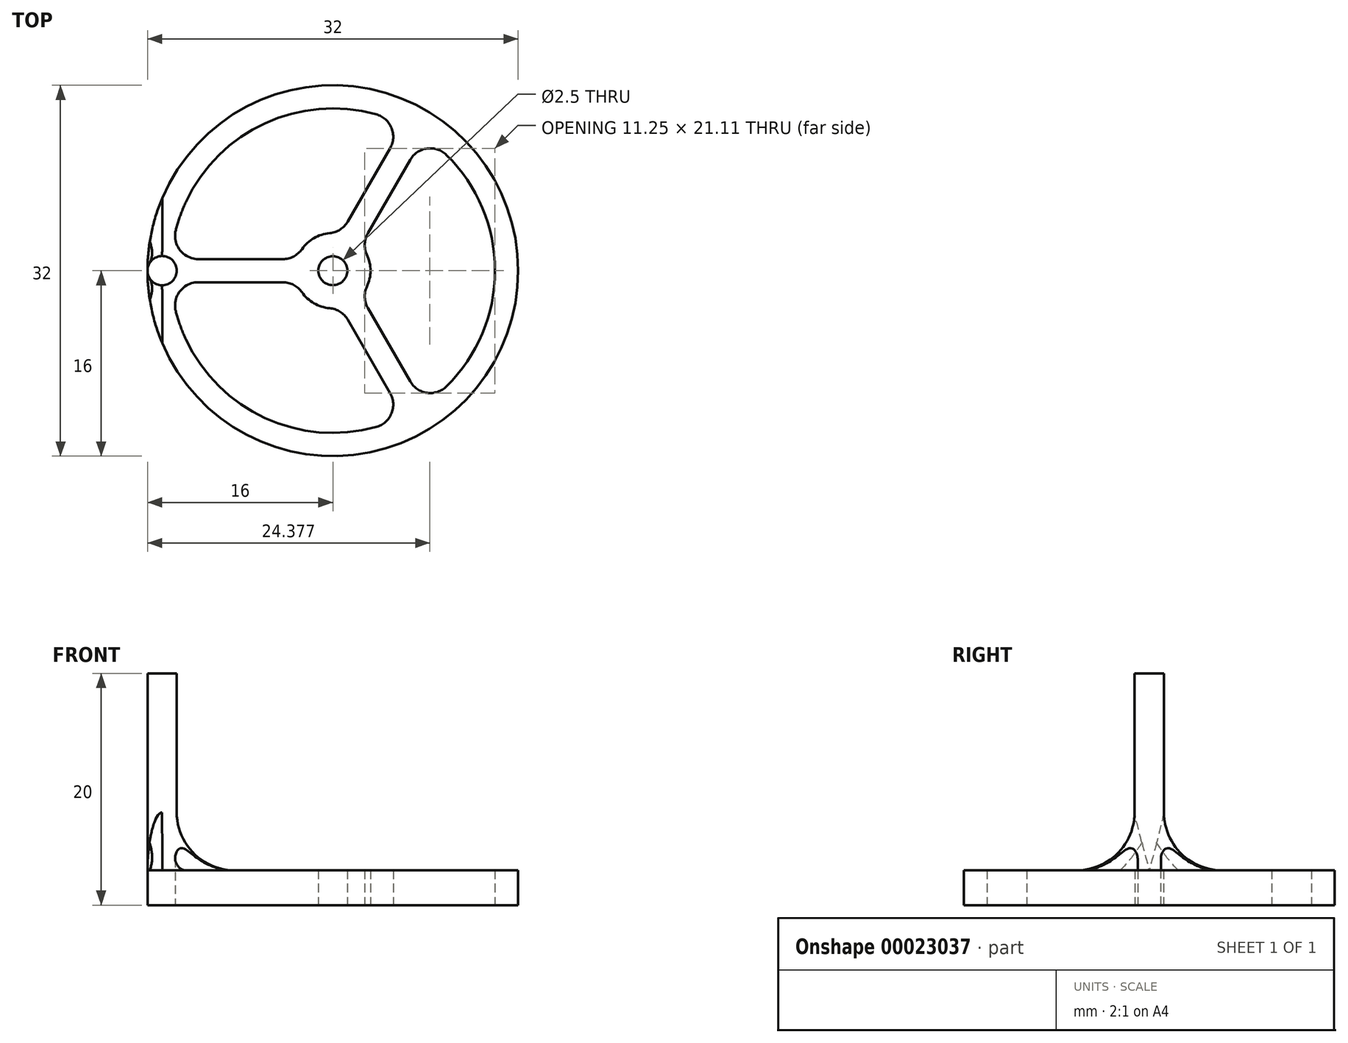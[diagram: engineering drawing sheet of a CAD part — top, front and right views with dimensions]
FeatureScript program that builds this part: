
annotation { "Feature Type Name" : "Feature", "Feature Type Description" : "" }
export const myFeature = defineFeature(function(context is Context, id is Id, definition is map)
    precondition{}
    {
        {
            var Q0;
            Q0=qCreatedBy(makeId("Top.planeOp"),FACE);
            var sketch = newSketch(context, id + "F0", { "sketchPlane" : qUnion([Q0])});
            skCircle(sketch, "E0", {"center": v(0, 0) * mm, "radius": 1.25 * mm});
            skCircle(sketch, "E1", {"center": v(0, 0) * mm, "radius": 14 * mm});
            skCircle(sketch, "E2", {"center": v(0, 0) * mm, "radius": 16 * mm});
            skCircle(sketch, "E3", {"center": v(0, 0) * mm, "radius": 3.25 * mm});
            skLineSegment(sketch, "E4", {"start": v(0, 1.25) * mm, "end": v(0, 3.25) * mm, "construction": true});
            skLineSegment(sketch, "E5", {"start": v(0, 14) * mm, "end": v(0, 16) * mm, "construction": true});
            skLineSegment(sketch, "E6", {"start": v(-3.1, -1) * mm, "end": v(-13.96, -1) * mm});
            skLineSegment(sketch, "E7", {"start": v(-3.1, 1) * mm, "end": v(-13.96, 1) * mm});
            skLineSegment(sketch, "E8", {"start": v(-8.53, -1) * mm, "end": v(-8.53, 1) * mm, "construction": true});
            skLineSegment(sketch, "E9", {"start": v(-16, 0) * mm, "end": v(16, 0) * mm, "construction": true});
            skPoint(sketch, "E10", {"position": v(-8.53, 0) * mm});
            skLineSegment(sketch, "E11.1.0", {"start": v(2.41, -2.18) * mm, "end": v(7.85, -11.6) * mm});
            skLineSegment(sketch, "E11.1.1", {"start": v(0.68, -3.18) * mm, "end": v(6.12, -12.6) * mm});
            skLineSegment(sketch, "E11.2.0", {"start": v(0.68, 3.18) * mm, "end": v(6.12, 12.6) * mm});
            skLineSegment(sketch, "E11.2.1", {"start": v(2.41, 2.18) * mm, "end": v(7.85, 11.6) * mm});
            skCircle(sketch, "E12", {"center": v(-14.74, 0) * mm, "radius": 1.26 * mm});
            skSolve(sketch);
        }
        {
            var Q0;
            Q0=makeQuery(id+"F0.imprint","IMPRINT",FACE,{"disambiguationData":[TD([[makeQuery(id+"F0.imprint","IMPRINT",EDGE,{"derivedFrom":sQuery(id+"F0.wireOp",EDGE,"E0")}),-1.0]])]});
            var Q1;
            {var subQ1=sQuery(id+"F0.wireOp",EDGE,"E11.2.0");Q1=makeQuery(id+"F0.imprint","IMPRINT",FACE,{"disambiguationData":[TD([[makeQuery(id+"F0.imprint","IMPRINT",EDGE,{"derivedFrom":subQ1}),-1.0]])]});}
            var Q2;
            {var subQ1=sQuery(id+"F0.wireOp",EDGE,"E11.1.0");Q2=makeQuery(id+"F0.imprint","IMPRINT",FACE,{"disambiguationData":[TD([[makeQuery(id+"F0.imprint","IMPRINT",EDGE,{"derivedFrom":subQ1}),-1.0]])]});}
            var Q3;
            {var subQ1=sQuery(id+"F0.wireOp",EDGE,"E2");Q3=makeQuery(id+"F0.imprint","IMPRINT",FACE,{"disambiguationData":[TD([[makeQuery(id+"F0.imprint","IMPRINT",EDGE,{"derivedFrom":subQ1}),1.0]])]});}
            var Q4;
            {var subQ0=sQuery(id+"F0.wireOp",EDGE,"E12");var subQ1=sQuery(id+"F0.wireOp",EDGE,"E1");var subQ3=makeQuery(id+"F0.imprint","INTERSECT",VERTEX,{"derivedFrom":[subQ1,sQuery(id+"F0.wireOp",EDGE,"E6"),subQ0]});Q4=makeQuery(id+"F0.imprint","IMPRINT",FACE,{"disambiguationData":[TD([[makeQuery(id+"F0.imprint","IMPRINT",EDGE,{"disambiguationData":[TD([[subQ3,1.0]])],"derivedFrom":subQ1}),1.0]])]});}
            var Q5;
            {var subQ3=sQuery(id+"F0.wireOp",EDGE,"E6");Q5=makeQuery(id+"F0.imprint","IMPRINT",FACE,{"disambiguationData":[TD([[makeQuery(id+"F0.imprint","IMPRINT",EDGE,{"derivedFrom":subQ3}),-1.0]])]});}
            var Q6;
            {var subQ0=sQuery(id+"F0.wireOp",EDGE,"E12");var subQ1=makeQuery(id+"F0.imprint","INTERSECT",VERTEX,{"derivedFrom":[sQuery(id+"F0.wireOp",EDGE,"E2"),subQ0]});Q6=makeQuery(id+"F0.imprint","IMPRINT",FACE,{"disambiguationData":[TD([[makeQuery(id+"F0.imprint","IMPRINT",EDGE,{"disambiguationData":[TD([[subQ1,1.0]])],"derivedFrom":subQ0}),1.0]])]});}
            extrude(context, id + "F1", {"entities" : qUnion([Q0, Q1, Q2, Q3, Q4, Q5, Q6]), "depth" : 3 * mm});
        }
        {
            var Q0;
            {var subQ0=sQuery(id+"F0.wireOp",EDGE,"E12");var subQ1=makeQuery(id+"F0.imprint","INTERSECT",VERTEX,{"derivedFrom":[sQuery(id+"F0.wireOp",EDGE,"E2"),subQ0]});Q0=makeQuery(id+"F0.imprint","IMPRINT",FACE,{"disambiguationData":[TD([[makeQuery(id+"F0.imprint","IMPRINT",EDGE,{"disambiguationData":[TD([[subQ1,1.0]])],"derivedFrom":subQ0}),1.0]])]});}
            var Q1;
            {var subQ0=sQuery(id+"F0.wireOp",EDGE,"E12");var subQ1=sQuery(id+"F0.wireOp",EDGE,"E1");var subQ3=makeQuery(id+"F0.imprint","INTERSECT",VERTEX,{"derivedFrom":[subQ1,sQuery(id+"F0.wireOp",EDGE,"E6"),subQ0]});Q1=makeQuery(id+"F0.imprint","IMPRINT",FACE,{"disambiguationData":[TD([[makeQuery(id+"F0.imprint","IMPRINT",EDGE,{"disambiguationData":[TD([[subQ3,1.0]])],"derivedFrom":subQ1}),1.0]])]});}
            extrude(context, id + "F2", {"entities" : qUnion([Q0, Q1]), "operationType" : NewBodyOperationType.ADD, "depth" : 20 * mm});
        }
        {
            var Q0;
            Q0=makeQuery(id+"F1.opExtrude","SWEPT_EDGE",EDGE,{"disambiguationData":[OSD([sQuery(id+"F0.wireOp",EDGE,"E1"),sQuery(id+"F0.wireOp",EDGE,"E6"),sQuery(id+"F0.wireOp",EDGE,"E12")])]});
            var Q1;
            Q1=makeQuery(id+"F1.opExtrude","SWEPT_EDGE",EDGE,{"disambiguationData":[OSD([sQuery(id+"F0.wireOp",EDGE,"E1"),sQuery(id+"F0.wireOp",EDGE,"E7"),sQuery(id+"F0.wireOp",EDGE,"E12")])]});
            var Q2;
            Q2=makeQuery(id+"F1.opExtrude","SWEPT_EDGE",EDGE,{"disambiguationData":[OSD([sQuery(id+"F0.wireOp",EDGE,"E1"),sQuery(id+"F0.wireOp",EDGE,"E11.2.0")])]});
            var Q3;
            Q3=makeQuery(id+"F1.opExtrude","SWEPT_EDGE",EDGE,{"disambiguationData":[OSD([sQuery(id+"F0.wireOp",EDGE,"E1"),sQuery(id+"F0.wireOp",EDGE,"E11.2.1")])]});
            var Q4;
            Q4=makeQuery(id+"F1.opExtrude","SWEPT_EDGE",EDGE,{"disambiguationData":[OSD([sQuery(id+"F0.wireOp",EDGE,"E1"),sQuery(id+"F0.wireOp",EDGE,"E11.1.0")])]});
            var Q5;
            Q5=makeQuery(id+"F1.opExtrude","SWEPT_EDGE",EDGE,{"disambiguationData":[OSD([sQuery(id+"F0.wireOp",EDGE,"E1"),sQuery(id+"F0.wireOp",EDGE,"E11.1.1")])]});
            var Q6;
            Q6=makeQuery(id+"F1.opExtrude","SWEPT_EDGE",EDGE,{"disambiguationData":[OSD([sQuery(id+"F0.wireOp",EDGE,"E3"),sQuery(id+"F0.wireOp",EDGE,"E6")])]});
            var Q7;
            Q7=makeQuery(id+"F1.opExtrude","SWEPT_EDGE",EDGE,{"disambiguationData":[OSD([sQuery(id+"F0.wireOp",EDGE,"E3"),sQuery(id+"F0.wireOp",EDGE,"E11.1.1")])]});
            var Q8;
            Q8=makeQuery(id+"F1.opExtrude","SWEPT_EDGE",EDGE,{"disambiguationData":[OSD([sQuery(id+"F0.wireOp",EDGE,"E3"),sQuery(id+"F0.wireOp",EDGE,"E11.1.0")])]});
            var Q9;
            Q9=makeQuery(id+"F1.opExtrude","SWEPT_EDGE",EDGE,{"disambiguationData":[OSD([sQuery(id+"F0.wireOp",EDGE,"E3"),sQuery(id+"F0.wireOp",EDGE,"E11.2.1")])]});
            var Q10;
            Q10=makeQuery(id+"F1.opExtrude","SWEPT_EDGE",EDGE,{"disambiguationData":[OSD([sQuery(id+"F0.wireOp",EDGE,"E3"),sQuery(id+"F0.wireOp",EDGE,"E11.2.0")])]});
            var Q11;
            Q11=makeQuery(id+"F1.opExtrude","SWEPT_EDGE",EDGE,{"disambiguationData":[OSD([sQuery(id+"F0.wireOp",EDGE,"E3"),sQuery(id+"F0.wireOp",EDGE,"E7")])]});
            fillet(context, id + "F3", {"entities" : qUnion([Q0, Q1, Q2, Q3, Q4, Q5, Q6, Q7, Q8, Q9, Q10, Q11]), "radius" : 2 * mm, "tangentPropagation" : true, "allowEdgeOverflow" : false});
        }
        {
            var Q0;
            Q0=makeQuery(id+"F2.boolean.opBoolean","INTERSECT",EDGE,{"disambiguationData":[OD(0.0)],"derivedFrom":[makeQuery(id+"F1.opExtrude","CAP_FACE",FACE,{"disambiguationData":[OSD([sQuery(id+"F0.wireOp",EDGE,"E0"),sQuery(id+"F0.wireOp",EDGE,"E1"),sQuery(id+"F0.wireOp",EDGE,"E2"),sQuery(id+"F0.wireOp",EDGE,"E3"),sQuery(id+"F0.wireOp",EDGE,"E6"),sQuery(id+"F0.wireOp",EDGE,"E7"),sQuery(id+"F0.wireOp",EDGE,"E11.1.0"),sQuery(id+"F0.wireOp",EDGE,"E11.1.1"),sQuery(id+"F0.wireOp",EDGE,"E11.2.0"),sQuery(id+"F0.wireOp",EDGE,"E11.2.1")])],"isStart":false}),makeQuery(id+"F2.opExtrude","SWEPT_FACE",FACE,{"disambiguationData":[OSD([sQuery(id+"F0.wireOp",EDGE,"E12")])]})]});
            fillet(context, id + "F4", {"entities" : qUnion([Q0]), "radius" : 5 * mm, "tangentPropagation" : true, "allowEdgeOverflow" : false});
        }
    });
